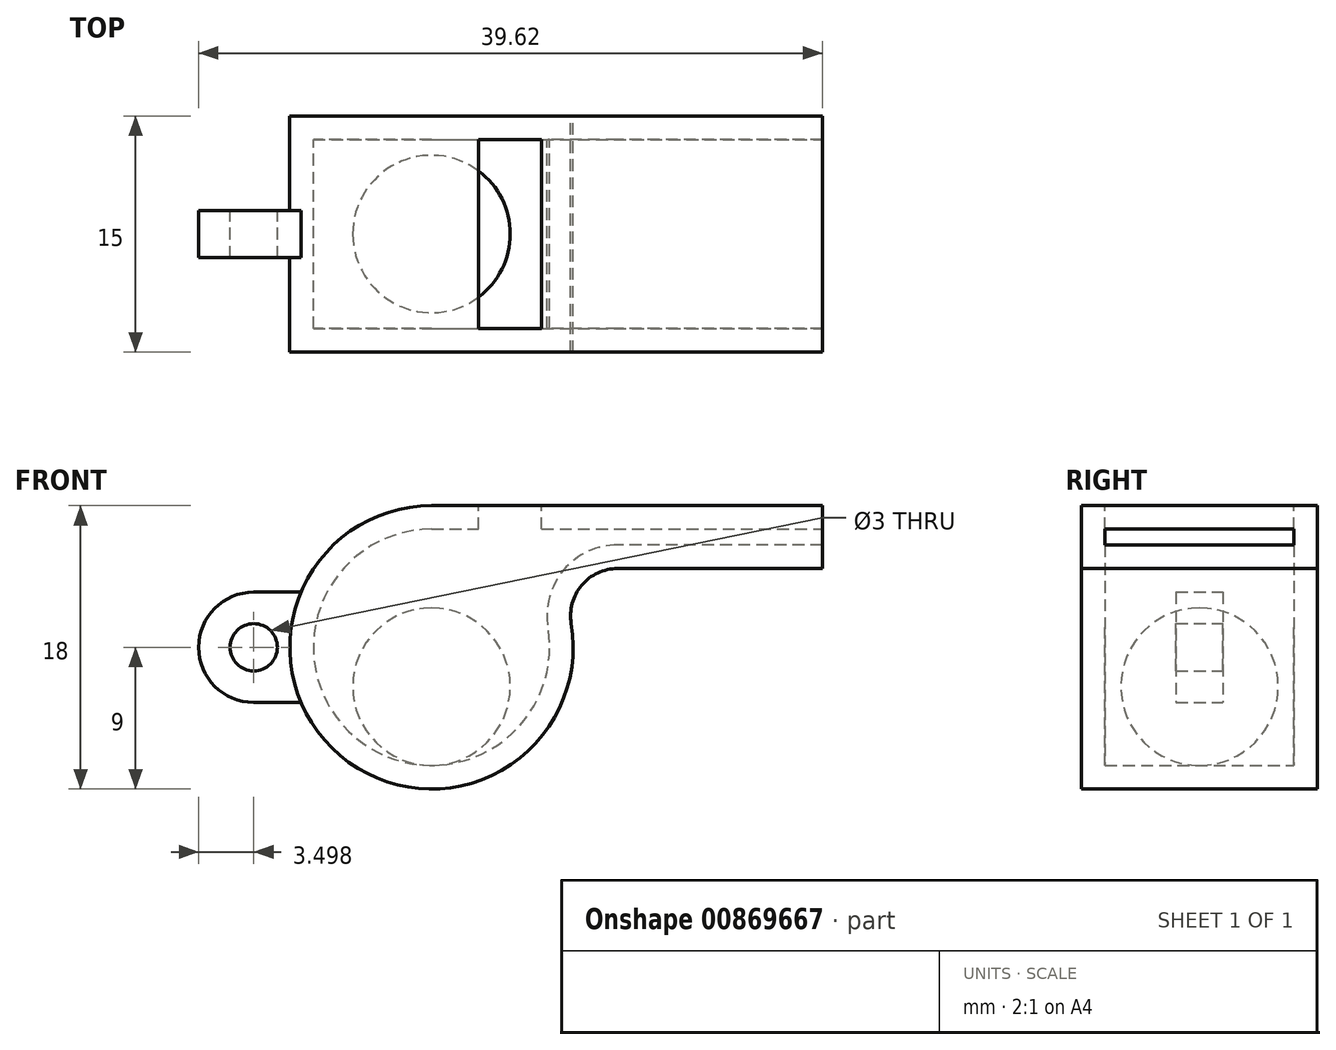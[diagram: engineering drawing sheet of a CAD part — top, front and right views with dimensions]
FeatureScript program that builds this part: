
annotation { "Feature Type Name" : "Feature", "Feature Type Description" : "" }
export const myFeature = defineFeature(function(context is Context, id is Id, definition is map)
    precondition{}
    {
        {
            var Q0;
            Q0=qCreatedBy(makeId("Front.planeOp"),FACE);
            var sketch = newSketch(context, id + "F0", { "sketchPlane" : qUnion([Q0])});
            skArc(sketch, "E0", {"start": v(0, 9) * mm, "mid": v(-5.8, -6.87) * mm, "end": v(8.87, 1.5) * mm});
            skLineSegment(sketch, "E1", {"start": v(0, 9) * mm, "end": v(24.83, 9) * mm});
            skLineSegment(sketch, "E2", {"start": v(24.83, 9) * mm, "end": v(24.83, 5) * mm});
            skLineSegment(sketch, "E3", {"start": v(24.83, 5) * mm, "end": v(11.83, 5) * mm});
            skPoint(sketch, "E4.visualSharp", {"position": v(7.48, 5) * mm});
            skArc(sketch, "E4.filletArc", {"start": v(11.83, 5) * mm, "mid": v(9.54, 3.94) * mm, "end": v(8.87, 1.5) * mm});
            skSolve(sketch);
        }
        {
            var Q0;
            Q0=makeQuery(id+"F0.imprint","IMPRINT",FACE,{"disambiguationData":[TD([[makeQuery(id+"F0.imprint","IMPRINT",EDGE,{"derivedFrom":sQuery(id+"F0.wireOp",EDGE,"E0")}),1.0]])]});
            extrude(context, id + "F1", {"entities" : qUnion([Q0]), "endBound" : BoundingType.SYMMETRIC, "depth" : 15 * mm, "offsetDistance" : 25 * mm});
        }
        {
            var Q0;
            Q0=makeQuery(id+"F1.opExtrude","SWEPT_FACE",FACE,{"disambiguationData":[OSD([sQuery(id+"F0.wireOp",EDGE,"E2")])]});
            shell(context, id + "F2", {"entities" : qUnion([Q0]), "thickness" : 1.5 * mm});
        }
        {
            var Q0;
            Q0=makeQuery(id+"F1.opExtrude","SWEPT_FACE",FACE,{"disambiguationData":[OSD([sQuery(id+"F0.wireOp",EDGE,"E1")])]});
            var sketch = newSketch(context, id + "F3", { "sketchPlane" : qUnion([Q0])});
            skLineSegment(sketch, "E5.bottom", {"start": v(3, 6) * mm, "end": v(7, 6) * mm});
            skLineSegment(sketch, "E5.top", {"start": v(3, -6) * mm, "end": v(7, -6) * mm});
            skLineSegment(sketch, "E5.left", {"start": v(3, 6) * mm, "end": v(3, -6) * mm});
            skLineSegment(sketch, "E5.right", {"start": v(7, 6) * mm, "end": v(7, -6) * mm});
            skSolve(sketch);
        }
        {
            var Q0;
            Q0=makeQuery(id+"F3.imprint","IMPRINT",FACE,{"disambiguationData":[TD([[makeQuery(id+"F3.imprint","IMPRINT",EDGE,{"derivedFrom":sQuery(id+"F3.wireOp",EDGE,"E5.bottom")}),-1.0]])]});
            extrude(context, id + "F4", {"entities" : qUnion([Q0]), "operationType" : NewBodyOperationType.REMOVE, "oppositeDirection" : true, "depth" : 1.5 * mm, "offsetDistance" : 25 * mm});
        }
        {
            var Q0;
            Q0=qCreatedBy(makeId("Front.planeOp"),FACE);
            var sketch = newSketch(context, id + "F5", { "sketchPlane" : qUnion([Q0])});
            skArc(sketch, "E6", {"start": v(-11.3, 3.5) * mm, "mid": v(-14.8, 0) * mm, "end": v(-11.3, -3.5) * mm});
            skLineSegment(sketch, "E7", {"start": v(-11.3, 3.5) * mm, "end": v(-8.3, 3.5) * mm});
            skLineSegment(sketch, "E8", {"start": v(-11.3, -3.5) * mm, "end": v(-8.3, -3.5) * mm});
            skCircle(sketch, "E9", {"center": v(-11.3, 0) * mm, "radius": 1.5 * mm});
            skLineSegment(sketch, "E10", {"start": v(-8.3, -3.5) * mm, "end": v(-8.3, 3.5) * mm});
            skSolve(sketch);
        }
        {
            var Q0;
            Q0 = qSketchRegion(id + "F5", true);
            extrude(context, id + "F6", {"entities" : qUnion([Q0]), "operationType" : NewBodyOperationType.ADD, "endBound" : BoundingType.SYMMETRIC, "depth" : 3 * mm, "offsetDistance" : 25 * mm});
        }
        {
            var Q0;
            Q0=qCreatedBy(makeId("Front.planeOp"),FACE);
            var sketch = newSketch(context, id + "F7", { "sketchPlane" : qUnion([Q0])});
            skArc(sketch, "E11", {"start": v(0, 2.5) * mm, "mid": v(5, -2.5) * mm, "end": v(0, -7.5) * mm});
            skLineSegment(sketch, "E12", {"start": v(0, 2.5) * mm, "end": v(0, -7.5) * mm});
            skSolve(sketch);
        }
        {
            var Q0;
            Q0 = qSketchRegion(id + "F7", true);
            var Q1;
            Q1=sQuery(id+"F7.wireOp",EDGE,"E12");
            revolve(context, id + "F8", {"surfaceOperationType" : NewSurfaceOperationType.NEW, "entities" : qUnion([Q0]), "axis" : qUnion([Q1]), "revolveType" : RevolveType.FULL});
        }
    });
